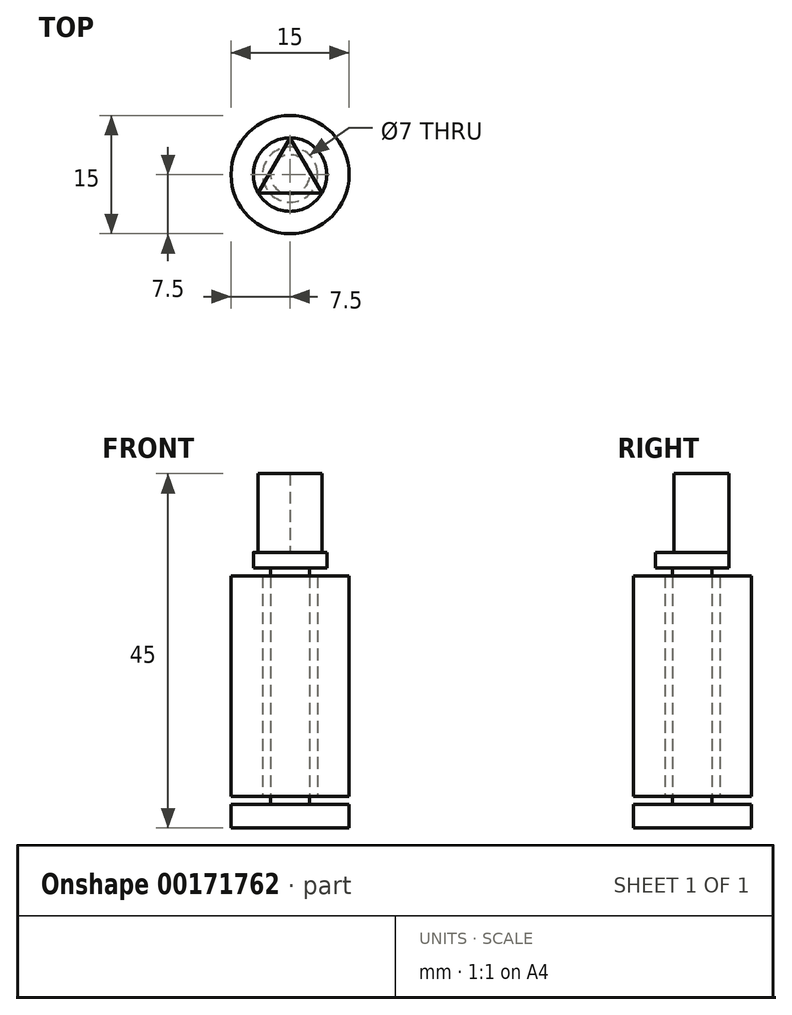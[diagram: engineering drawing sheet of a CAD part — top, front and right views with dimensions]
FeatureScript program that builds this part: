
annotation { "Feature Type Name" : "Feature", "Feature Type Description" : "" }
export const myFeature = defineFeature(function(context is Context, id is Id, definition is map)
    precondition{}
    {
        {
            var Q0;
            Q0=qCreatedBy(makeId("Top.planeOp"),FACE);
            var sketch = newSketch(context, id + "F0", { "sketchPlane" : qUnion([Q0])});
            skCircle(sketch, "E0", {"center": v(0, 0) * mm, "radius": 7.5 * mm});
            skSolve(sketch);
        }
        {
            var Q0;
            Q0 = qSketchRegion(id + "F0", true);
            extrude(context, id + "F1", {"entities" : qUnion([Q0]), "depth" : 3 * mm});
        }
        {
            var Q0;
            Q0=makeQuery(id+"F1.opExtrude","CAP_FACE",FACE,{"disambiguationData":[OSD([sQuery(id+"F0.wireOp",EDGE,"E0")])],"isStart":false});
            var sketch = newSketch(context, id + "F2", { "sketchPlane" : qUnion([Q0])});
            skCircle(sketch, "E1", {"center": v(0, 0) * mm, "radius": 2.5 * mm});
            skSolve(sketch);
        }
        {
            var Q0;
            Q0 = qSketchRegion(id + "F2", true);
            extrude(context, id + "F3", {"entities" : qUnion([Q0]), "operationType" : NewBodyOperationType.ADD, "depth" : 30 * mm});
        }
        {
            var Q0;
            Q0=makeQuery(id+"F3.opExtrude","CAP_FACE",FACE,{"disambiguationData":[OSD([sQuery(id+"F2.wireOp",EDGE,"E1")])],"isStart":false});
            var sketch = newSketch(context, id + "F4", { "sketchPlane" : qUnion([Q0])});
            skCircle(sketch, "E2", {"center": v(0, 0) * mm, "radius": 4.67 * mm});
            skLineSegment(sketch, "E3", {"start": v(0, 4.67) * mm, "end": v(-4.04, -2.33) * mm, "construction": true});
            skLineSegment(sketch, "E4", {"start": v(-4.04, -2.33) * mm, "end": v(4.04, -2.33) * mm, "construction": true});
            skLineSegment(sketch, "E5", {"start": v(4.04, -2.33) * mm, "end": v(0, 4.67) * mm, "construction": true});
            skSolve(sketch);
        }
        {
            var Q0;
            Q0 = qSketchRegion(id + "F4", true);
            extrude(context, id + "F5", {"entities" : qUnion([Q0]), "operationType" : NewBodyOperationType.ADD, "depth" : 2 * mm});
        }
        {
            var Q0;
            Q0=makeQuery(id+"F5.opExtrude","CAP_FACE",FACE,{"disambiguationData":[OSD([sQuery(id+"F4.wireOp",EDGE,"E2")])],"isStart":false});
            var sketch = newSketch(context, id + "F6", { "sketchPlane" : qUnion([Q0])});
            skLineSegment(sketch, "E6", {"start": v(0, 4.67) * mm, "end": v(-4.04, -2.33) * mm});
            skLineSegment(sketch, "E7", {"start": v(-4.04, -2.33) * mm, "end": v(4.04, -2.33) * mm});
            skLineSegment(sketch, "E8", {"start": v(4.04, -2.33) * mm, "end": v(0, 4.67) * mm});
            skSolve(sketch);
        }
        {
            var Q0;
            Q0 = qSketchRegion(id + "F6", true);
            extrude(context, id + "F7", {"entities" : qUnion([Q0]), "operationType" : NewBodyOperationType.ADD, "depth" : 10 * mm});
        }
        {
            var Q0;
            Q0=makeQuery(id+"F1.opExtrude","CAP_FACE",FACE,{"disambiguationData":[OSD([sQuery(id+"F0.wireOp",EDGE,"E0")])],"isStart":false});
            cPlane(context, id + "F8", {"entities" : qUnion([Q0]), "cplaneType" : CPlaneType.OFFSET, "offset" : 1 * mm, "width" : 150 * mm, "height" : 150 * mm});
        }
        {
            var Q0;
            Q0=qCreatedBy(id+"F8.planeOp",FACE);
            var sketch = newSketch(context, id + "F9", { "sketchPlane" : qUnion([Q0])});
            skCircle(sketch, "E9", {"center": v(0, 0) * mm, "radius": 7.5 * mm});
            skCircle(sketch, "E10", {"center": v(0, 0) * mm, "radius": 3.5 * mm});
            skSolve(sketch);
        }
        {
            var Q0;
            Q0 = qSketchRegion(id + "F9", true);
            extrude(context, id + "F10", {"entities" : qUnion([Q0]), "depth" : 28 * mm});
        }
    });
